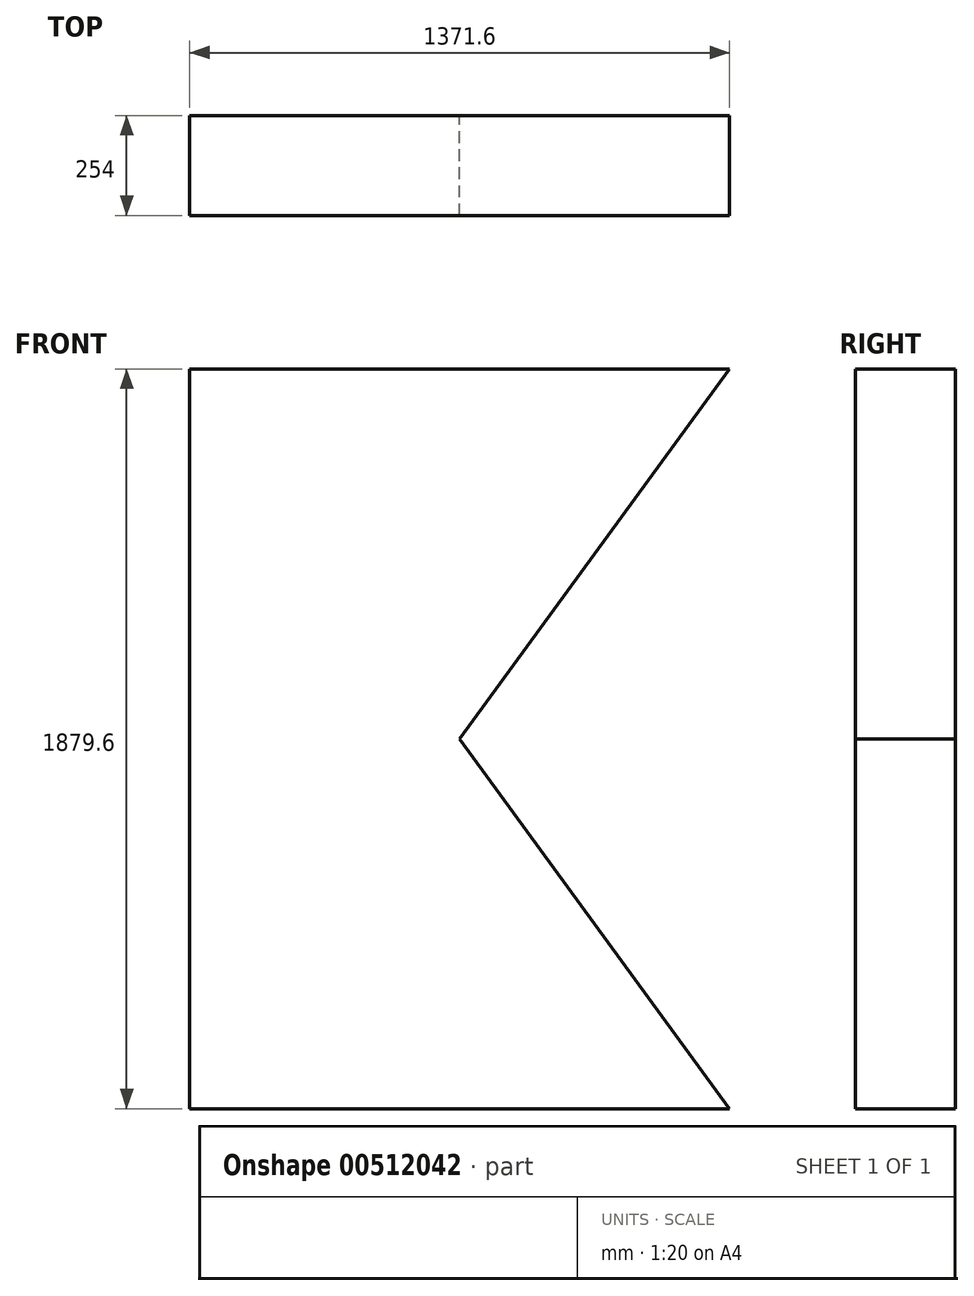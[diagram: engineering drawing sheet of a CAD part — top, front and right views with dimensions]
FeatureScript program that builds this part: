
annotation { "Feature Type Name" : "Feature", "Feature Type Description" : "" }
export const myFeature = defineFeature(function(context is Context, id is Id, definition is map)
    precondition{}
    {
        {
            var Q0;
            Q0=qCreatedBy(makeId("Front.planeOp"),FACE);
            var sketch = newSketch(context, id + "F0", { "sketchPlane" : qUnion([Q0])});
            skLineSegment(sketch, "E0.bottom", {"start": v(-685.8, -939.8) * mm, "end": v(685.8, -939.8) * mm});
            skLineSegment(sketch, "E0.top", {"start": v(-685.8, 939.8) * mm, "end": v(685.8, 939.8) * mm});
            skLineSegment(sketch, "E0.left", {"start": v(-685.8, -939.8) * mm, "end": v(-685.8, 939.8) * mm});
            skLineSegment(sketch, "E0.right", {"start": v(685.8, -939.8) * mm, "end": v(685.8, 939.8) * mm});
            skLineSegment(sketch, "E1.bottom", {"start": v(685.8, 939.8) * mm, "end": v(685.8, 939.8) * mm});
            skLineSegment(sketch, "E1.top", {"start": v(685.8, -939.8) * mm, "end": v(685.8, -939.8) * mm});
            skLineSegment(sketch, "E1.left", {"start": v(685.8, 939.8) * mm, "end": v(685.8, -939.8) * mm});
            skLineSegment(sketch, "E1.right", {"start": v(685.8, 939.8) * mm, "end": v(685.8, -939.8) * mm});
            skLineSegment(sketch, "E2", {"start": v(685.8, 939.8) * mm, "end": v(-685.8, -939.8) * mm});
            skLineSegment(sketch, "E3", {"start": v(-685.8, 939.8) * mm, "end": v(685.8, -939.8) * mm});
            skSolve(sketch);
        }
        {
            var Q0;
            {var subQ0=sQuery(id+"F0.wireOp",EDGE,"E0.left");Q0=makeQuery(id+"F0.imprint","IMPRINT",FACE,{"disambiguationData":[TD([[makeQuery(id+"F0.imprint","IMPRINT",EDGE,{"derivedFrom":subQ0}),-1.0]])]});}
            var Q1;
            {var subQ0=sQuery(id+"F0.wireOp",EDGE,"E0.top");Q1=makeQuery(id+"F0.imprint","IMPRINT",FACE,{"disambiguationData":[TD([[makeQuery(id+"F0.imprint","IMPRINT",EDGE,{"derivedFrom":subQ0}),-1.0]])]});}
            var Q2;
            {var subQ0=sQuery(id+"F0.wireOp",EDGE,"E1.right");Q2=makeQuery(id+"F0.imprint","IMPRINT",FACE,{"disambiguationData":[TD([[makeQuery(id+"F0.imprint","IMPRINT",EDGE,{"derivedFrom":subQ0}),-1.0]])]});}
            var Q3;
            {var subQ0=sQuery(id+"F0.wireOp",EDGE,"E0.bottom");Q3=makeQuery(id+"F0.imprint","IMPRINT",FACE,{"disambiguationData":[TD([[makeQuery(id+"F0.imprint","IMPRINT",EDGE,{"derivedFrom":subQ0}),1.0]])]});}
            extrude(context, id + "F1", {"entities" : qUnion([Q0, Q1, Q2, Q3]), "depth" : 254 * mm});
        }
    });
